# Revit family: BIM_Model_Sanimat_1000_50_D
name_source: partatom
category: Mechanical Equipment
revit_build: Autodesk Revit 2018 (Build: 20170223_1515(x64)
units: mm (PartAtom-declared; Revit-internal decimal feet)

## family parameters
Always vertical = Yes
Cut with Voids When Loaded = No
Part Type = Normal
Room Calculation Point = No
Round Connector Dimension = Use Radius
Shared = No
Work Plane-Based = No

## types (1)
- Sanimat 1000 D
    Cable Length (m) = 4 + 1.5
    Capacity (m3/hr) = 56 m³
    DN 100 Inflow Adapter = 50 mm  [stored 0.164042 ft]
    Description = Flood-Proof, Single Lifting Station, for the removal of wastewater and sewage from areas below the sewer level in accordance with EN12050-1
    Discharge Connection = Sleeve 4'' DN 100
    Discharge Flange DN 80 = 40 mm  [stored 0.131234 ft]
    Flexible Connector = 50 mm  [stored 0.164042 ft]
    Head (m) = 9 mm  [stored 0.0295276 ft]
    Impeller = Cast Iron EN-GJL-250
    Inflow DN 100 = 50 mm  [stored 0.164042 ft]
    Inflow DN 100 (with adaptor fitted) = 50 mm  [stored 0.164042 ft]
    Inflow DN 100 (with blanking plate fitted) = 50 mm  [stored 0.164042 ft]
    Inflow DN 150 = 75 mm
    Inflow DN 70 = 35 mm  [stored 0.114829 ft]
    Inflow/Hand Membrane Pump DN 40 = 20 mm  [stored 0.0656168 ft]
    Manufacturer = Sulzer
    Model = Lifting Station Type ABS Sanimat 1000
    Motor Housing = Cast Iron EN-GJL-250
    Motor Power (kW) = P1=1.77 P2=1.40
    Product Specification Link = http://www.sulzer.com
    Rated Current (A) = 3.5
    Rated Voltage (V) = 400 3~
    Rotor Shaft = Stainless steel 1.4021 (AISI 420)
    Speed (r/min) = 1450
    Tank Material = Polyethylene
    Vent/Inflow DN 70 = 35 mm  [stored 0.114829 ft]
    Volute = Polyethylene
    Weight (Kg) = 55

note: [stored X ft] marks values corroborated as IEEE doubles in the binary element streams (Revit-internal decimal feet)

## geometry (parser evidence)
native form markers: Sweep x3
no freeform markers — native parametric forms only
